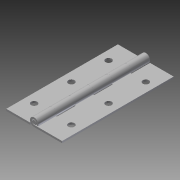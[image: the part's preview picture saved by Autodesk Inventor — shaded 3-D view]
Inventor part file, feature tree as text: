
AUTODESK INVENTOR PART (.ipt)
format: ipt  version: 2014 (Build 180170000, 170)  size: 330,240 bytes
history: native  units: in
note: dims shown in document units (in); Inventor stores cm internally (conversion verified against a paired STEP export)
features: extrude x6, sketch x5, imported_body x3, projected_geometry x3, other x2, chamfer x1
ambient origin geometry x8: Origin, YZ Plane, XZ Plane, XY Plane, X Axis, Y Axis, Z Axis, Center Point
bodies: Body1 (feature_tree), Body2 (feature_tree), Body3 (feature_tree)
feature tree (20):
  other  "LPattern1"
  other  "15665A319 (1)1"
  extrude  "Extrusion2"  Depth=1.5in
  extrude  "Extrusion3"  Depth=1.0in TaperAngle=0.0deg
  extrude  "Extrusion4"  Depth=0.164in
  extrude  "Extrusion5"  Depth=0.5in
  extrude  "Extrusion6"  Depth=1.5in
  chamfer  "Chamfer1"  Distance=1.75in
  extrude  "Extrude5"  Depth=1.0in TaperAngle=0.0deg
  imported_body  "Base1"
  imported_body  "Base2"
  imported_body  "Base3"
  sketch  "Sketch2"  dims[d5=1.5in d6=9.0in]
  sketch  "Sketch3"  dims[d7=1.0in d8=0.0in d9=9.0in d10=0.0in]
  projected_geometry  "Projected Loop1"
  projected_geometry  "Projected Loop2"
  sketch  "Sketch4"  dims[d11=9.0in d12=0.0in d13=0.164in]
  sketch  "Sketch5"  dims[d14=0.25in d15=0.5in]
  sketch  "Sketch6"  dims[d18=10.25in d19=0.0in d20=1.5in d21=1.75in d22=10.25in d23=0.0in d24=1.1811in d26=1.0in d27=0.3937in d29=1.0in]
  projected_geometry  "Projected Loop3"
